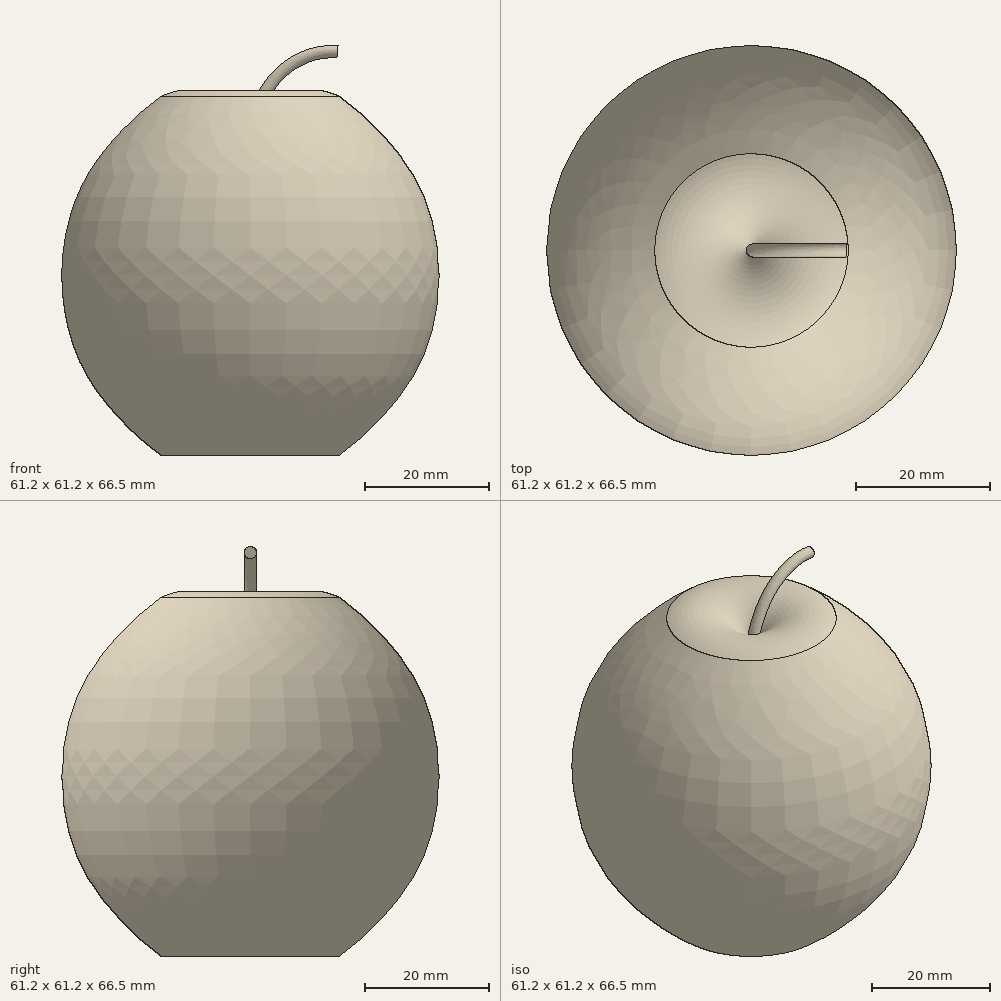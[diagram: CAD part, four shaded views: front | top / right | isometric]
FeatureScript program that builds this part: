
annotation { "Feature Type Name" : "Feature", "Feature Type Description" : "" }
export const myFeature = defineFeature(function(context is Context, id is Id, definition is map)
    precondition{}
    {
        {
            var Q0;
            Q0=qCreatedBy(makeId("Front.planeOp"),FACE);
            var sketch = newSketch(context, id + "F0", { "sketchPlane" : qUnion([Q0])});
            skLineSegment(sketch, "E0", {"start": v(0, 0) * mm, "end": v(0, 65) * mm});
            skArc(sketch, "E1", {"start": v(14.44, 3.39) * mm, "mid": v(32.5, 32.5) * mm, "end": v(14.44, 61.61) * mm, "construction": true});
            skArc(sketch, "E2", {"start": v(14.44, 61.61) * mm, "mid": v(4.73, 61.15) * mm, "end": v(0, 52.66) * mm});
            skArc(sketch, "E3", {"start": v(0, 12.34) * mm, "mid": v(4.73, 3.85) * mm, "end": v(14.44, 3.39) * mm});
            skFitSpline(sketch, "E4", {"points": [v(14.44, 61.61) * mm, v(23.78, 52.66) * mm, v(28.58, 44.2) * mm, v(30.61, 32.5) * mm, v(28.58, 20.8) * mm, v(23.78, 12.34) * mm, v(14.44, 3.39) * mm], "startDerivative": vector(61.17, -43.62) * mm, "endDerivative": vector(-61.17, -43.62) * mm});
            skLineSegment(sketch, "E5", {"start": v(30.61, 32.5) * mm, "end": v(0, 32.5) * mm, "construction": true});
            skSolve(sketch);
        }
        {
            var Q0;
            {var subQ0=sQuery(id+"F0.wireOp",EDGE,"E2");Q0=makeQuery(id+"F0.imprint","IMPRINT",FACE,{"disambiguationData":[TD([[makeQuery(id+"F0.imprint","IMPRINT",EDGE,{"derivedFrom":subQ0}),1.0]])]});}
            var Q1;
            Q1=sQuery(id+"F0.wireOp",EDGE,"E0");
            revolve(context, id + "F1", {"entities" : qUnion([Q0]), "axis" : qUnion([Q1]), "revolveType" : RevolveType.FULL});
        }
        {
            var Q0;
            Q0=qCreatedBy(makeId("Front.planeOp"),FACE);
            var sketch = newSketch(context, id + "F2", { "sketchPlane" : qUnion([Q0])});
            skFitSpline(sketch, "E6", {"points": [v(0, 42.37) * mm, v(0, 48.51) * mm, v(0, 54.65) * mm, v(1.2, 59.87) * mm, v(3.51, 63.86) * mm, v(5.82, 66.19) * mm, v(9, 68.03) * mm, v(14.13, 68.84) * mm], "startDerivative": vector(0.74, 37.46) * mm, "endDerivative": vector(41.82, -2.94) * mm});
            skSolve(sketch);
        }
        {
            var Q0;
            Q0=sQuery(id+"F2.wireOp",EDGE,"E6");
            var Q1;
            Q1=sQuery(id+"F2.wireOp",VERTEX,"E6.end");
            cPlane(context, id + "F3", {"entities" : qUnion([Q0, Q1]), "cplaneType" : CPlaneType.CURVE_POINT, "offset" : 150 * mm, "width" : 150 * mm, "height" : 150 * mm});
        }
        {
            var Q0;
            Q0=qCreatedBy(id+"F3.planeOp",FACE);
            var sketch = newSketch(context, id + "F4", { "sketchPlane" : qUnion([Q0])});
            skCircle(sketch, "E7", {"center": v(0, 69.66) * mm, "radius": 1 * mm});
            skSolve(sketch);
        }
        {
            var Q0;
            Q0=makeQuery(id+"F4.imprint","IMPRINT",FACE,{"disambiguationData":[TD([[makeQuery(id+"F4.imprint","IMPRINT",EDGE,{"derivedFrom":sQuery(id+"F4.wireOp",EDGE,"E7")}),1.0]])]});
            var Q1;
            Q1=sQuery(id+"F2.wireOp",EDGE,"E6");
            sweep(context, id + "F5", {"operationType" : NewBodyOperationType.ADD, "profiles" : qUnion([Q0]), "path" : qUnion([Q1])});
        }
    });
